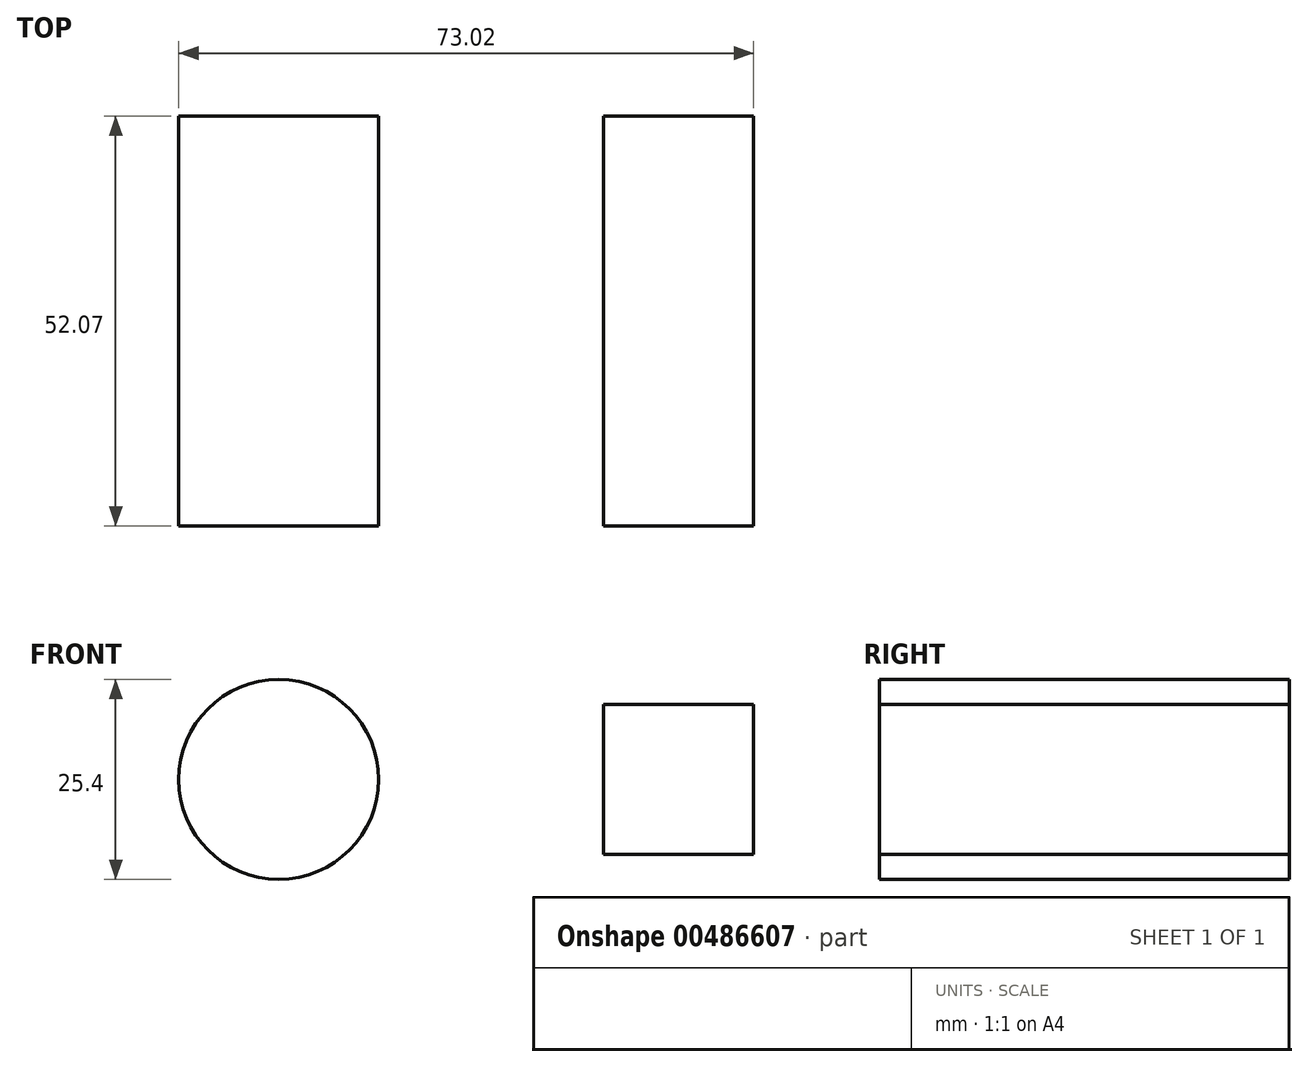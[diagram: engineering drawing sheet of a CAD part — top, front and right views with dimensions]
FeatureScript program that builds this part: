
annotation { "Feature Type Name" : "Feature", "Feature Type Description" : "" }
export const myFeature = defineFeature(function(context is Context, id is Id, definition is map)
    precondition{}
    {
        {
            var Q0;
            Q0=qCreatedBy(makeId("Front.planeOp"),FACE);
            var sketch = newSketch(context, id + "F0", { "sketchPlane" : qUnion([Q0])});
            skLineSegment(sketch, "E0", {"start": v(6.35, 0) * mm, "end": v(-6.35, -22) * mm});
            skLineSegment(sketch, "E1", {"start": v(-6.35, -22) * mm, "end": v(19.05, -22) * mm});
            skLineSegment(sketch, "E2", {"start": v(19.05, -22) * mm, "end": v(6.35, 0) * mm});
            skLineSegment(sketch, "E3.bottom", {"start": v(-22.22, 9.52) * mm, "end": v(-41.27, 9.52) * mm});
            skLineSegment(sketch, "E3.top", {"start": v(-22.22, -9.53) * mm, "end": v(-41.27, -9.53) * mm});
            skLineSegment(sketch, "E3.left", {"start": v(-22.22, 9.52) * mm, "end": v(-22.22, -9.53) * mm});
            skLineSegment(sketch, "E3.right", {"start": v(-41.27, 9.52) * mm, "end": v(-41.27, -9.53) * mm});
            skLineSegment(sketch, "E4", {"start": v(-31.75, 0) * mm, "end": v(-82.55, 0) * mm});
            skPoint(sketch, "E4.startSnap0", {"position": v(-31.75, -9.53) * mm});
            skCircle(sketch, "E5", {"center": v(-82.55, 0) * mm, "radius": 12.7 * mm});
            skLineSegment(sketch, "E6", {"start": v(0, -48.66) * mm, "end": v(44.45, -48.66) * mm});
            skLineSegment(sketch, "E7.bottom", {"start": v(44.45, -48.66) * mm, "end": v(-107.95, -48.66) * mm});
            skLineSegment(sketch, "E7.top", {"start": v(44.45, 34.07) * mm, "end": v(-107.95, 34.07) * mm});
            skLineSegment(sketch, "E7.left", {"start": v(44.45, -48.66) * mm, "end": v(44.45, 34.07) * mm});
            skLineSegment(sketch, "E7.right", {"start": v(-107.95, -48.66) * mm, "end": v(-107.95, 34.07) * mm});
            skSolve(sketch);
        }
        {
            var Q0;
            Q0=makeQuery(id+"F0.imprint","IMPRINT",FACE,{"disambiguationData":[TD([[makeQuery(id+"F0.imprint","IMPRINT",EDGE,{"derivedFrom":sQuery(id+"F0.wireOp",EDGE,"E5")}),1.0]])]});
            var Q1;
            {var subQ1=sQuery(id+"F0.wireOp",EDGE,"E3.bottom");Q1=makeQuery(id+"F0.imprint","IMPRINT",FACE,{"disambiguationData":[TD([[makeQuery(id+"F0.imprint","IMPRINT",EDGE,{"derivedFrom":subQ1}),1.0]])]});}
            extrude(context, id + "F1", {"entities" : qUnion([Q0, Q1]), "depth" : 52.07 * mm});
        }
    });
